# Revit family: Track-Sliding-Krown_Lab-Ragnar
name_source: partatom
category: Doors
revit_build: Autodesk Revit MEP 2012 (Build: 20110916_2132(x64)
units: mm (PartAtom-declared; Revit-internal decimal feet)

## types (2) — shared parameters
Date Last Modified = 9/2/15
Description = See Part Description
Equipment Abbreviation = DR
Family Version = 1.0
Manufacturer = Krown Lab
Model = See Part Number
Model Disclaimer = For More Information, Contact Krown Lab
Product Documentation Link = https://krownlab.com
Product Page URL = http://www.krownlab.com
Type Comments = To Modify the Panel, edit the nested Panel Family and reload into the Door
URL = http://www.krownlab.com

## per-type parameters (varying)
| type | Handle Material | Product Material | z Handle Material | z Handle Material Rail | z Trolley Material | z Type |
| Stainless Steel, Brushed | Stainless Steel - Krown Lab - Brushed | Stainless Steel - Krown Lab - Brushed | Stainless Steel - Krown Lab - Brushed | Stainless Steel - Krown Lab - Brushed | Stainless Steel - Krown Lab - Brushed | 2 |
| Stainless Steel, Black | Stainless Steel - Krown Lab - Black | Stainless Steel - Krown Lab - Black | Stainless Steel - Krown Lab - Black | Stainless Steel - Krown Lab - Black | Stainless Steel - Krown Lab - Black | 1 |

## geometry (parser evidence)
native form markers: Blend x3, Sweep x6
no freeform markers — native parametric forms only
